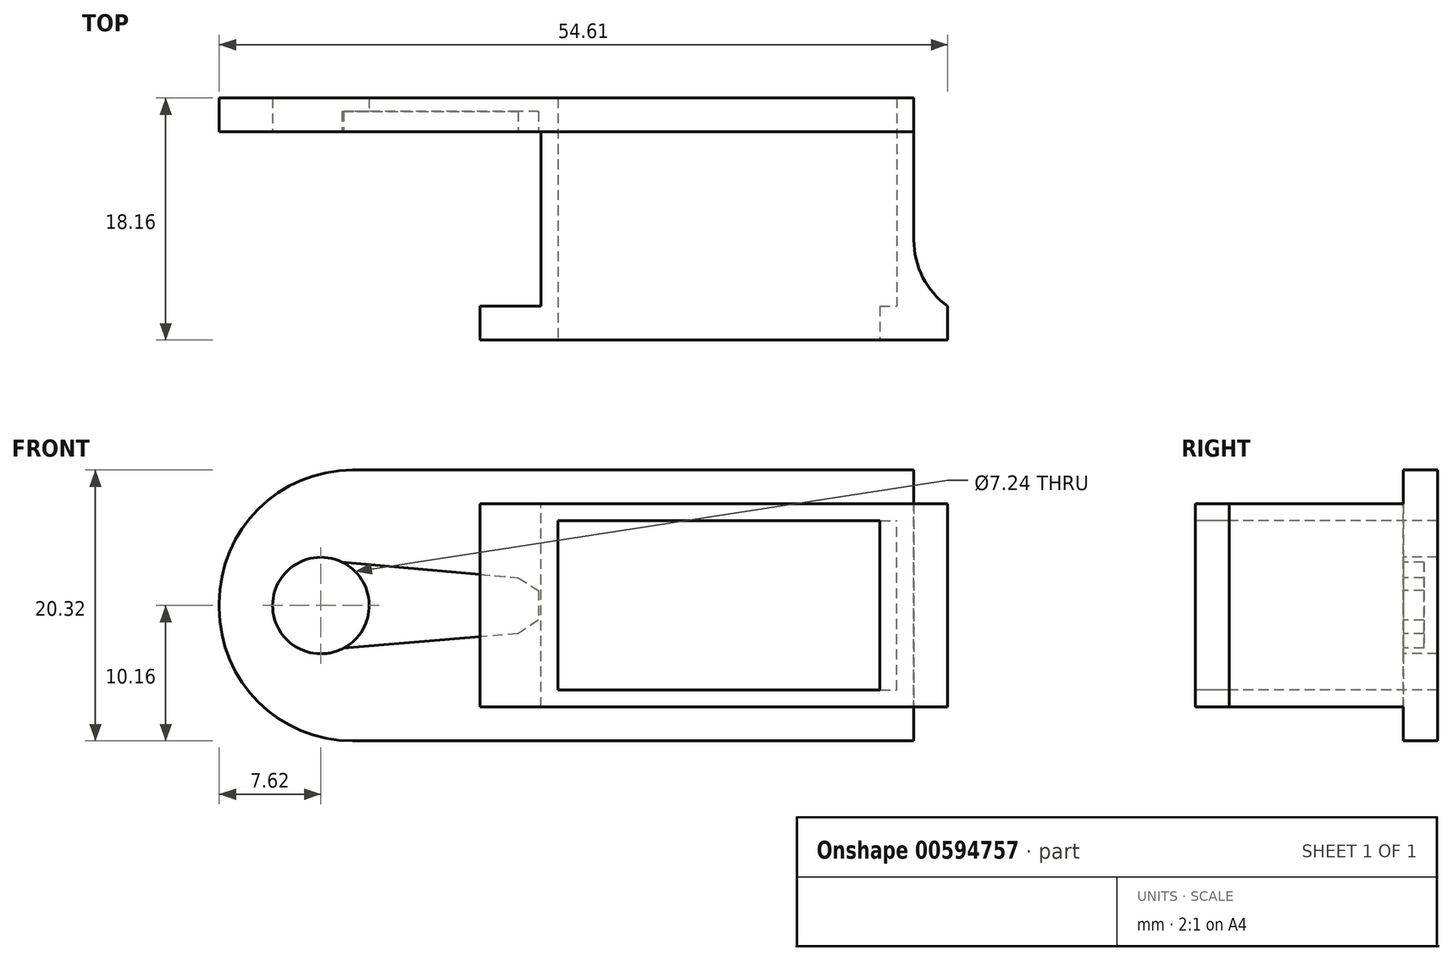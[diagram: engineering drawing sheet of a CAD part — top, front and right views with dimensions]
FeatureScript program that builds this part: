
annotation { "Feature Type Name" : "Feature", "Feature Type Description" : "" }
export const myFeature = defineFeature(function(context is Context, id is Id, definition is map)
    precondition{}
    {
        {
            var Q0;
            Q0=qCreatedBy(makeId("Front.planeOp"),FACE);
            var sketch = newSketch(context, id + "F0", { "sketchPlane" : qUnion([Q0])});
            skLineSegment(sketch, "E0.bottom", {"start": v(15.24, -10.16) * mm, "end": v(-15.24, -10.16) * mm});
            skLineSegment(sketch, "E0.top", {"start": v(15.24, 10.16) * mm, "end": v(-15.24, 10.16) * mm});
            skLineSegment(sketch, "E0.left", {"start": v(15.24, -10.16) * mm, "end": v(15.24, 10.16) * mm});
            skLineSegment(sketch, "E0.right", {"start": v(-15.24, -10.16) * mm, "end": v(-15.24, 10.16) * mm});
            skPoint(sketch, "E0.middle", {"position": v(0, 0) * mm});
            skSolve(sketch);
        }
        {
            var Q0;
            Q0 = qSketchRegion(id + "F0", true);
            extrude(context, id + "F1", {"entities" : qUnion([Q0]), "depth" : 2.54 * mm, "offsetDistance" : 25.4 * mm});
        }
        {
            var Q0;
            Q0=makeQuery(id+"F1.opExtrude","CAP_FACE",FACE,{"disambiguationData":[OSD([sQuery(id+"F0.wireOp",EDGE,"E0.bottom"),sQuery(id+"F0.wireOp",EDGE,"E0.top"),sQuery(id+"F0.wireOp",EDGE,"E0.left"),sQuery(id+"F0.wireOp",EDGE,"E0.right")])],"isStart":false});
            var sketch = newSketch(context, id + "F2", { "sketchPlane" : qUnion([Q0])});
            skCircle(sketch, "E1", {"center": v(-7.62, 0) * mm, "radius": 3.62 * mm});
            skSolve(sketch);
        }
        {
            var Q0;
            Q0=makeQuery(id+"F2.imprint","IMPRINT",FACE,{"disambiguationData":[TD([[makeQuery(id+"F2.imprint","IMPRINT",EDGE,{"derivedFrom":sQuery(id+"F2.wireOp",EDGE,"E1")}),-1.0]])]});
            var sketch = newSketch(context, id + "F3", { "sketchPlane" : qUnion([Q0])});
            skLineSegment(sketch, "E2", {"start": v(-6.09, 3.27) * mm, "end": v(7.15, 2.08) * mm});
            skLineSegment(sketch, "E3", {"start": v(7.15, 2.08) * mm, "end": v(8.7, 1.14) * mm});
            skLineSegment(sketch, "E4", {"start": v(8.7, -1.1) * mm, "end": v(7.15, -2.1) * mm});
            skLineSegment(sketch, "E5", {"start": v(7.15, -2.1) * mm, "end": v(-5.91, -3.2) * mm});
            skLineSegment(sketch, "E6", {"start": v(-5.91, -3.2) * mm, "end": v(-6.09, 3.27) * mm});
            skLineSegment(sketch, "E7", {"start": v(8.7, 1.14) * mm, "end": v(8.7, -1.1) * mm});
            skSolve(sketch);
        }
        {
            var Q0;
            Q0 = qSketchRegion(id + "F2", true);
            extrude(context, id + "F4", {"entities" : qUnion([Q0]), "operationType" : NewBodyOperationType.REMOVE, "oppositeDirection" : true, "depth" : 25.4 * mm, "offsetDistance" : 25.4 * mm});
        }
        {
            var Q0;
            Q0 = qSketchRegion(id + "F3", true);
            extrude(context, id + "F5", {"entities" : qUnion([Q0]), "operationType" : NewBodyOperationType.REMOVE, "oppositeDirection" : true, "depth" : 1.52 * mm, "offsetDistance" : 25.4 * mm});
        }
        {
            var Q0;
            Q0=makeQuery(id+"F1.opExtrude","SWEPT_FACE",FACE,{"disambiguationData":[OSD([sQuery(id+"F0.wireOp",EDGE,"E0.left")])]});
            extrude(context, id + "F6", {"entities" : qUnion([Q0]), "operationType" : NewBodyOperationType.ADD, "depth" : 21.59 * mm, "offsetDistance" : 25.4 * mm});
        }
        {
            var Q0;
            {var subQ0=sQuery(id+"F0.wireOp",EDGE,"E0.left");Q0=makeQuery(id+"F6.boolean.opBoolean","MERGE",FACE,{"derivedFrom":[makeQuery(id+"F1.opExtrude","CAP_FACE",FACE,{"disambiguationData":[OSD([sQuery(id+"F0.wireOp",EDGE,"E0.bottom"),sQuery(id+"F0.wireOp",EDGE,"E0.top"),subQ0,sQuery(id+"F0.wireOp",EDGE,"E0.right")])],"isStart":false}),makeQuery(id+"F6.opExtrude","SWEPT_FACE",FACE,{"disambiguationData":[OSD([subQ0]),TDD([makeQuery(id+"F1.opExtrude","CAP_EDGE",EDGE,{"disambiguationData":[OSD([subQ0])],"isStart":false})])]})]});}
            var sketch = newSketch(context, id + "F7", { "sketchPlane" : qUnion([Q0])});
            skLineSegment(sketch, "E8.bottom", {"start": v(36.83, -7.62) * mm, "end": v(8.89, -7.62) * mm});
            skLineSegment(sketch, "E8.top", {"start": v(36.83, 7.62) * mm, "end": v(8.89, 7.62) * mm});
            skLineSegment(sketch, "E8.left", {"start": v(36.83, -7.62) * mm, "end": v(36.83, 7.62) * mm});
            skLineSegment(sketch, "E8.right", {"start": v(8.89, -7.62) * mm, "end": v(8.89, 7.62) * mm});
            skPoint(sketch, "E8.middle", {"position": v(22.86, 0) * mm});
            skSolve(sketch);
        }
        {
            var Q0;
            Q0 = qSketchRegion(id + "F7", true);
            extrude(context, id + "F8", {"entities" : qUnion([Q0]), "operationType" : NewBodyOperationType.ADD, "depth" : 15.62 * mm, "offsetDistance" : 25.4 * mm});
        }
        {
            var Q0;
            Q0=makeQuery(id+"F8.opExtrude","CAP_FACE",FACE,{"disambiguationData":[OSD([sQuery(id+"F7.wireOp",EDGE,"E8.bottom"),sQuery(id+"F7.wireOp",EDGE,"E8.top"),sQuery(id+"F7.wireOp",EDGE,"E8.left"),sQuery(id+"F7.wireOp",EDGE,"E8.right")])],"isStart":false});
            var sketch = newSketch(context, id + "F9", { "sketchPlane" : qUnion([Q0])});
            skLineSegment(sketch, "E9", {"start": v(36.83, 0) * mm, "end": v(22.86, 0) * mm});
            skPoint(sketch, "E9.endSnap0", {"position": v(8.9, 0) * mm});
            skLineSegment(sketch, "E10.bottom", {"start": v(10.16, -6.35) * mm, "end": v(35.56, -6.35) * mm});
            skLineSegment(sketch, "E10.top", {"start": v(10.16, 6.35) * mm, "end": v(35.56, 6.35) * mm});
            skLineSegment(sketch, "E10.left", {"start": v(10.16, -6.35) * mm, "end": v(10.16, 6.35) * mm});
            skLineSegment(sketch, "E10.right", {"start": v(35.56, -6.35) * mm, "end": v(35.56, 6.35) * mm});
            skPoint(sketch, "E10.middle", {"position": v(22.86, 0) * mm});
            skSolve(sketch);
        }
        {
            var Q0;
            Q0 = qSketchRegion(id + "F9", true);
            extrude(context, id + "F10", {"entities" : qUnion([Q0]), "operationType" : NewBodyOperationType.REMOVE, "oppositeDirection" : true, "depth" : 25.4 * mm, "offsetDistance" : 25.4 * mm});
        }
        {
            var Q0;
            Q0=makeQuery(id+"F8.opExtrude","SWEPT_FACE",FACE,{"disambiguationData":[OSD([sQuery(id+"F7.wireOp",EDGE,"E8.right")])]});
            var sketch = newSketch(context, id + "F11", { "sketchPlane" : qUnion([Q0])});
            skLineSegment(sketch, "E11.bottom", {"start": v(18.16, 7.62) * mm, "end": v(15.62, 7.62) * mm});
            skLineSegment(sketch, "E11.top", {"start": v(18.16, -7.62) * mm, "end": v(15.62, -7.62) * mm});
            skLineSegment(sketch, "E11.left", {"start": v(18.16, 7.62) * mm, "end": v(18.16, -7.62) * mm});
            skLineSegment(sketch, "E11.right", {"start": v(15.62, 7.62) * mm, "end": v(15.62, -7.62) * mm});
            skSolve(sketch);
        }
        {
            var Q0;
            Q0 = qSketchRegion(id + "F11", true);
            extrude(context, id + "F12", {"entities" : qUnion([Q0]), "operationType" : NewBodyOperationType.ADD, "depth" : 4.57 * mm, "offsetDistance" : 25.4 * mm});
        }
        {
            var Q0;
            Q0=makeQuery(id+"F8.boolean.opBoolean","MERGE",FACE,{"derivedFrom":[makeQuery(id+"F6.opExtrude","CAP_FACE",FACE,{"disambiguationData":[OSD([sQuery(id+"F0.wireOp",EDGE,"E0.left")])],"isStart":false}),makeQuery(id+"F8.opExtrude","SWEPT_FACE",FACE,{"disambiguationData":[OSD([sQuery(id+"F7.wireOp",EDGE,"E8.left")])]})]});
            var sketch = newSketch(context, id + "F13", { "sketchPlane" : qUnion([Q0])});
            skLineSegment(sketch, "E12.bottom", {"start": v(-18.16, 7.62) * mm, "end": v(-15.62, 7.62) * mm});
            skLineSegment(sketch, "E12.top", {"start": v(-18.16, -7.62) * mm, "end": v(-15.62, -7.62) * mm});
            skLineSegment(sketch, "E12.left", {"start": v(-18.16, 7.62) * mm, "end": v(-18.16, -7.62) * mm});
            skLineSegment(sketch, "E12.right", {"start": v(-15.62, 7.62) * mm, "end": v(-15.62, -7.62) * mm});
            skSolve(sketch);
        }
        {
            var Q0;
            Q0=makeQuery(id+"F13.imprint","IMPRINT",FACE,{"disambiguationData":[TD([[makeQuery(id+"F13.imprint","IMPRINT",EDGE,{"derivedFrom":sQuery(id+"F13.wireOp",EDGE,"E12.bottom")}),-1.0]])]});
            extrude(context, id + "F14", {"entities" : qUnion([Q0]), "operationType" : NewBodyOperationType.ADD, "endBound" : BoundingType.SYMMETRIC, "depth" : 5.08 * mm, "offsetDistance" : 25.4 * mm});
        }
        {
            var Q0;
            Q0=makeQuery(id+"F1.opExtrude","SWEPT_EDGE",EDGE,{"disambiguationData":[OSD([sQuery(id+"F0.wireOp",EDGE,"E0.top"),sQuery(id+"F0.wireOp",EDGE,"E0.right")])]});
            var Q1;
            Q1=makeQuery(id+"F1.opExtrude","SWEPT_EDGE",EDGE,{"disambiguationData":[OSD([sQuery(id+"F0.wireOp",EDGE,"E0.bottom"),sQuery(id+"F0.wireOp",EDGE,"E0.right")])]});
            fillet(context, id + "F15", {"entities" : qUnion([Q0, Q1]), "radius" : 10 * mm, "tangentPropagation" : true, "allowEdgeOverflow" : false});
        }
        {
            var Q0;
            Q0=makeQuery(id+"F12.opExtrude","CAP_EDGE",EDGE,{"disambiguationData":[OSD([sQuery(id+"F11.wireOp",EDGE,"E11.right")])],"isStart":true});
            var Q1;
            Q1=makeQuery(id+"F14.boolean.opBoolean","INTERSECT",EDGE,{"derivedFrom":[makeQuery(id+"F8.boolean.opBoolean","MERGE",FACE,{"derivedFrom":[makeQuery(id+"F6.opExtrude","CAP_FACE",FACE,{"disambiguationData":[OSD([sQuery(id+"F0.wireOp",EDGE,"E0.left")])],"isStart":false}),makeQuery(id+"F8.opExtrude","SWEPT_FACE",FACE,{"disambiguationData":[OSD([sQuery(id+"F7.wireOp",EDGE,"E8.left")])]})]}),makeQuery(id+"F14.opExtrude","SWEPT_FACE",FACE,{"disambiguationData":[OSD([sQuery(id+"F13.wireOp",EDGE,"E12.right")])]})]});
            fillet(context, id + "F16", {"entities" : qUnion([Q0, Q1]), "radius" : 6.13 * mm, "tangentPropagation" : true, "allowEdgeOverflow" : false});
        }
    });
